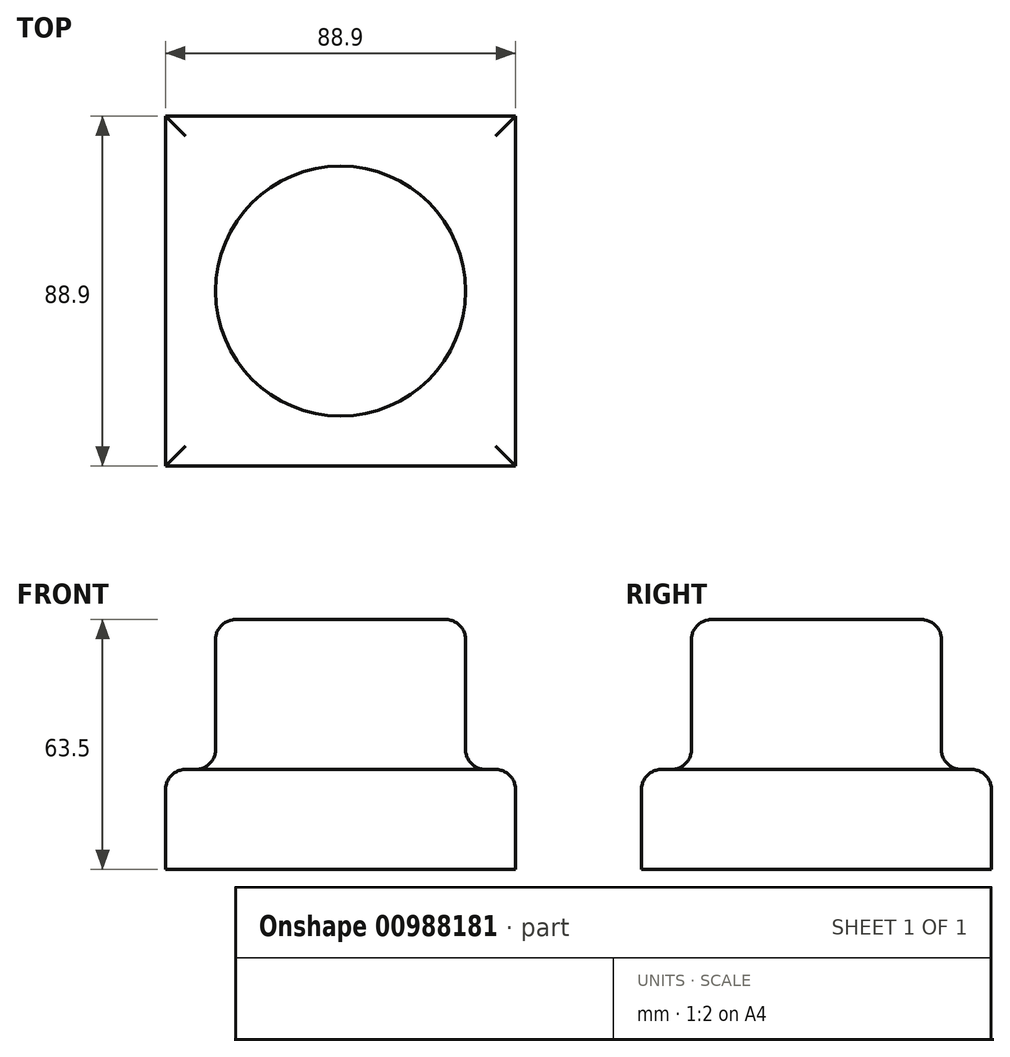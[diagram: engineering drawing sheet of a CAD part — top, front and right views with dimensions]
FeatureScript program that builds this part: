
annotation { "Feature Type Name" : "Feature", "Feature Type Description" : "" }
export const myFeature = defineFeature(function(context is Context, id is Id, definition is map)
    precondition{}
    {
        {
            var Q0;
            Q0=qCreatedBy(makeId("Top.planeOp"),FACE);
            var sketch = newSketch(context, id + "F0", { "sketchPlane" : qUnion([Q0])});
            skLineSegment(sketch, "E0.bottom", {"start": v(44.45, -44.45) * mm, "end": v(-44.45, -44.45) * mm});
            skLineSegment(sketch, "E0.top", {"start": v(44.45, 44.45) * mm, "end": v(-44.45, 44.45) * mm});
            skLineSegment(sketch, "E0.left", {"start": v(44.45, -44.45) * mm, "end": v(44.45, 44.45) * mm});
            skLineSegment(sketch, "E0.right", {"start": v(-44.45, -44.45) * mm, "end": v(-44.45, 44.45) * mm});
            skPoint(sketch, "E0.middle", {"position": v(0, 0) * mm});
            skSolve(sketch);
        }
        {
            var Q0;
            Q0=makeQuery(id+"F0.imprint","IMPRINT",FACE,{"disambiguationData":[TD([[makeQuery(id+"F0.imprint","IMPRINT",EDGE,{"derivedFrom":sQuery(id+"F0.wireOp",EDGE,"E0.bottom")}),-1.0]])]});
            extrude(context, id + "F1", {"entities" : qUnion([Q0]), "depth" : 25.4 * mm, "offsetDistance" : 25.4 * mm});
        }
        {
            var Q0;
            Q0=makeQuery(id+"F1.opExtrude","CAP_FACE",FACE,{"disambiguationData":[OSD([sQuery(id+"F0.wireOp",EDGE,"E0.bottom"),sQuery(id+"F0.wireOp",EDGE,"E0.top"),sQuery(id+"F0.wireOp",EDGE,"E0.left"),sQuery(id+"F0.wireOp",EDGE,"E0.right")])],"isStart":false});
            var sketch = newSketch(context, id + "F2", { "sketchPlane" : qUnion([Q0])});
            skCircle(sketch, "E1", {"center": v(0, 0) * mm, "radius": 31.75 * mm});
            skSolve(sketch);
        }
        {
            var Q0;
            Q0=makeQuery(id+"F2.imprint","IMPRINT",FACE,{"disambiguationData":[TD([[makeQuery(id+"F2.imprint","IMPRINT",EDGE,{"derivedFrom":sQuery(id+"F2.wireOp",EDGE,"E1")}),1.0]])]});
            extrude(context, id + "F3", {"entities" : qUnion([Q0]), "operationType" : NewBodyOperationType.ADD, "depth" : 38.1 * mm, "offsetDistance" : 25.4 * mm});
        }
        {
            var Q0;
            Q0=makeQuery(id+"F3.opExtrude","CAP_EDGE",EDGE,{"disambiguationData":[OSD([sQuery(id+"F2.wireOp",EDGE,"E1")])],"isStart":false});
            var Q1;
            Q1=makeQuery(id+"F3.opExtrude","CAP_EDGE",EDGE,{"disambiguationData":[OSD([sQuery(id+"F2.wireOp",EDGE,"E1")])],"isStart":true});
            var Q2;
            Q2=makeQuery(id+"F1.opExtrude","CAP_EDGE",EDGE,{"disambiguationData":[OSD([sQuery(id+"F0.wireOp",EDGE,"E0.left")])],"isStart":false});
            var Q3;
            Q3=makeQuery(id+"F1.opExtrude","CAP_FACE",FACE,{"disambiguationData":[OSD([sQuery(id+"F0.wireOp",EDGE,"E0.bottom"),sQuery(id+"F0.wireOp",EDGE,"E0.top"),sQuery(id+"F0.wireOp",EDGE,"E0.left"),sQuery(id+"F0.wireOp",EDGE,"E0.right")])],"isStart":false});
            fillet(context, id + "F4", {"entities" : qUnion([Q0, Q1, Q2, Q3]), "radius" : 5.08 * mm, "tangentPropagation" : true, "allowEdgeOverflow" : false});
        }
    });
